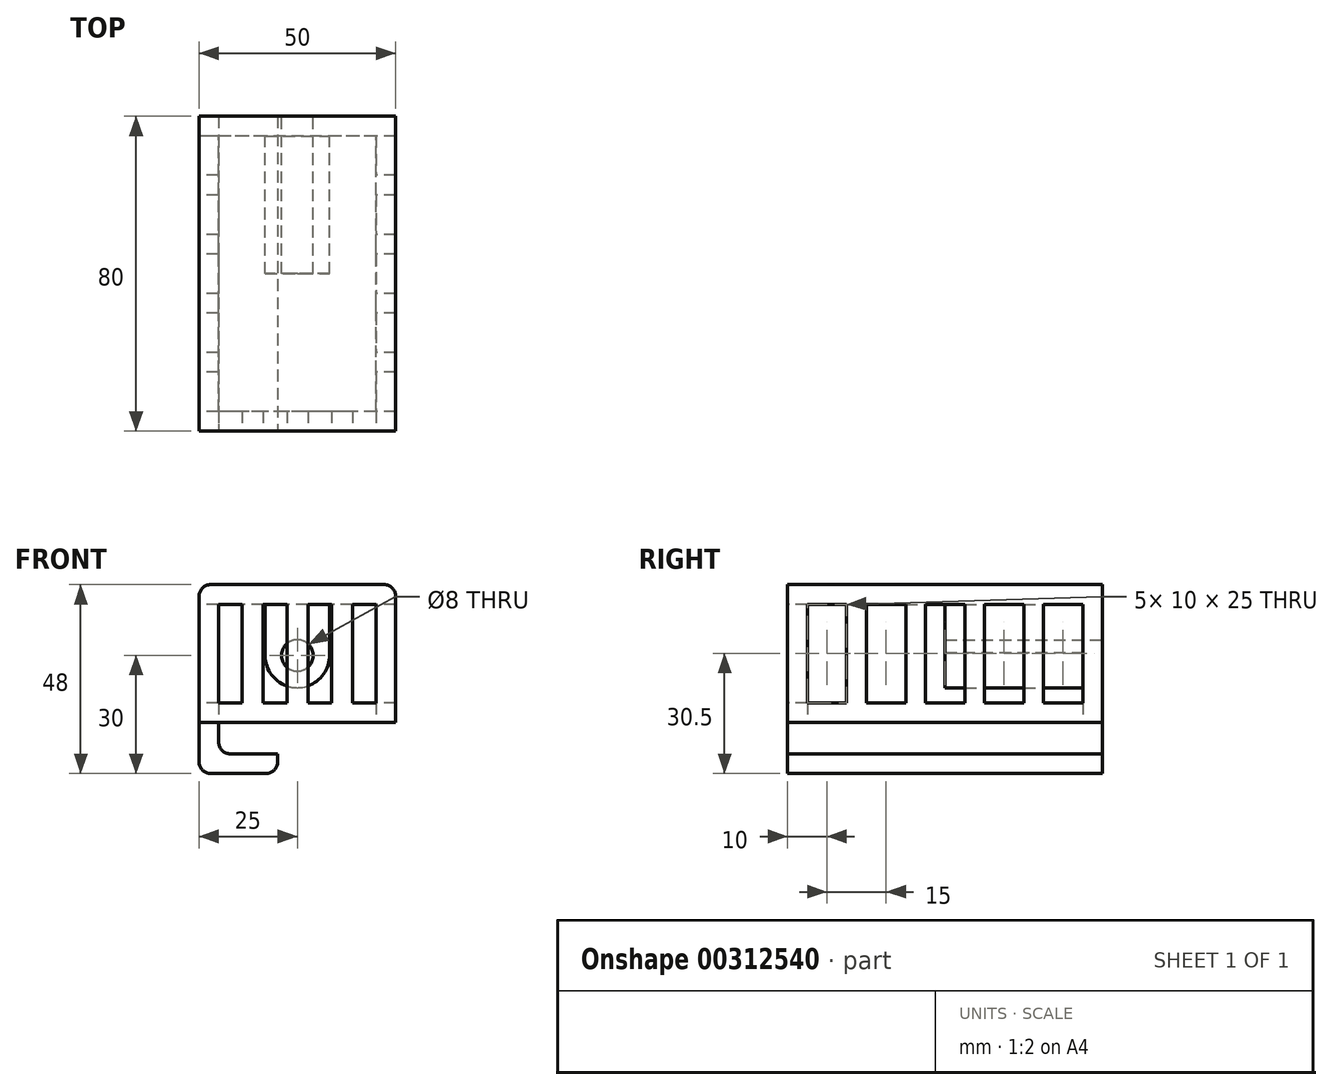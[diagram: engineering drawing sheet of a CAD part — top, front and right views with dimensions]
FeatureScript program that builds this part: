
annotation { "Feature Type Name" : "Feature", "Feature Type Description" : "" }
export const myFeature = defineFeature(function(context is Context, id is Id, definition is map)
    precondition{}
    {
        {
            var Q0;
            Q0=qCreatedBy(makeId("Top.planeOp"),FACE);
            var sketch = newSketch(context, id + "F0", { "sketchPlane" : qUnion([Q0])});
            skLineSegment(sketch, "E0.bottom", {"start": v(-50, 80) * mm, "end": v(0, 80) * mm});
            skLineSegment(sketch, "E0.top", {"start": v(-50, 0) * mm, "end": v(0, 0) * mm});
            skLineSegment(sketch, "E0.left", {"start": v(-50, 80) * mm, "end": v(-50, 0) * mm});
            skLineSegment(sketch, "E0.right", {"start": v(0, 80) * mm, "end": v(0, 0) * mm});
            skSolve(sketch);
        }
        {
            var Q0;
            Q0=qSketchRegion(id+"F0",true);
            extrude(context, id + "F1", {"entities" : qUnion([Q0]), "depth" : 35 * mm});
        }
        {
            var Q0;
            Q0=makeQuery(id+"F1.opExtrude","CAP_FACE",FACE,{"disambiguationData":[OSD([sQuery(id+"F0.wireOp",EDGE,"E0.bottom"),sQuery(id+"F0.wireOp",EDGE,"E0.top"),sQuery(id+"F0.wireOp",EDGE,"E0.left"),sQuery(id+"F0.wireOp",EDGE,"E0.right")])],"isStart":true});
            var sketch = newSketch(context, id + "F2", { "sketchPlane" : qUnion([Q0])});
            skLineSegment(sketch, "E1.bottom", {"start": v(-5, -5) * mm, "end": v(-45, -5) * mm});
            skLineSegment(sketch, "E1.top", {"start": v(-5, -75) * mm, "end": v(-45, -75) * mm});
            skLineSegment(sketch, "E1.left", {"start": v(-5, -5) * mm, "end": v(-5, -75) * mm});
            skLineSegment(sketch, "E1.right", {"start": v(-45, -5) * mm, "end": v(-45, -75) * mm});
            skSolve(sketch);
        }
        {
            var Q0;
            Q0=makeQuery(id+"F2.imprint","IMPRINT",FACE,{"disambiguationData":[TD([[makeQuery(id+"F2.imprint","IMPRINT",EDGE,{"derivedFrom":sQuery(id+"F2.wireOp",EDGE,"E1.bottom")}),1.0]])]});
            extrude(context, id + "F3", {"entities" : qUnion([Q0]), "operationType" : NewBodyOperationType.REMOVE, "oppositeDirection" : true, "depth" : 30 * mm});
        }
        {
            var Q0;
            Q0=makeQuery(id+"F1.opExtrude","SWEPT_FACE",FACE,{"disambiguationData":[OSD([sQuery(id+"F0.wireOp",EDGE,"E0.bottom")])]});
            var sketch = newSketch(context, id + "F4", { "sketchPlane" : qUnion([Q0])});
            skCircle(sketch, "E2", {"center": v(25, 17) * mm, "radius": 4 * mm});
            skSolve(sketch);
        }
        {
            var Q0;
            Q0=makeQuery(id+"F4.imprint","IMPRINT",FACE,{"disambiguationData":[TD([[makeQuery(id+"F4.imprint","IMPRINT",EDGE,{"derivedFrom":sQuery(id+"F4.wireOp",EDGE,"E2")}),1.0]])]});
            extrude(context, id + "F5", {"entities" : qUnion([Q0]), "operationType" : NewBodyOperationType.REMOVE, "endBound" : BoundingType.UP_TO_NEXT, "oppositeDirection" : true, "depth" : 25 * mm});
        }
        {
            var Q0;
            Q0=makeQuery(id+"F1.opExtrude","SWEPT_FACE",FACE,{"disambiguationData":[OSD([sQuery(id+"F0.wireOp",EDGE,"E0.left")])]});
            var sketch = newSketch(context, id + "F6", { "sketchPlane" : qUnion([Q0])});
            skLineSegment(sketch, "E3.bottom", {"start": v(-75, 30) * mm, "end": v(-65, 30) * mm});
            skLineSegment(sketch, "E3.top", {"start": v(-75, 5) * mm, "end": v(-65, 5) * mm});
            skLineSegment(sketch, "E3.left", {"start": v(-75, 30) * mm, "end": v(-75, 5) * mm});
            skLineSegment(sketch, "E3.right", {"start": v(-65, 30) * mm, "end": v(-65, 5) * mm});
            skLineSegment(sketch, "E4.1.0.0", {"start": v(-50, 30) * mm, "end": v(-50, 5) * mm});
            skLineSegment(sketch, "E4.1.0.1", {"start": v(-60, 30) * mm, "end": v(-50, 30) * mm});
            skLineSegment(sketch, "E4.1.0.2", {"start": v(-60, 30) * mm, "end": v(-60, 5) * mm});
            skLineSegment(sketch, "E4.1.0.3", {"start": v(-60, 5) * mm, "end": v(-50, 5) * mm});
            skLineSegment(sketch, "E4.2.0.0", {"start": v(-35, 30) * mm, "end": v(-35, 5) * mm});
            skLineSegment(sketch, "E4.2.0.1", {"start": v(-45, 30) * mm, "end": v(-35, 30) * mm});
            skLineSegment(sketch, "E4.2.0.2", {"start": v(-45, 30) * mm, "end": v(-45, 5) * mm});
            skLineSegment(sketch, "E4.2.0.3", {"start": v(-45, 5) * mm, "end": v(-35, 5) * mm});
            skLineSegment(sketch, "E4.3.0.0", {"start": v(-20, 30) * mm, "end": v(-20, 5) * mm});
            skLineSegment(sketch, "E4.3.0.1", {"start": v(-30, 30) * mm, "end": v(-20, 30) * mm});
            skLineSegment(sketch, "E4.3.0.2", {"start": v(-30, 30) * mm, "end": v(-30, 5) * mm});
            skLineSegment(sketch, "E4.3.0.3", {"start": v(-30, 5) * mm, "end": v(-20, 5) * mm});
            skLineSegment(sketch, "E4.4.0.0", {"start": v(-5, 30) * mm, "end": v(-5, 5) * mm});
            skLineSegment(sketch, "E4.4.0.1", {"start": v(-15, 30) * mm, "end": v(-5, 30) * mm});
            skLineSegment(sketch, "E4.4.0.2", {"start": v(-15, 30) * mm, "end": v(-15, 5) * mm});
            skLineSegment(sketch, "E4.4.0.3", {"start": v(-15, 5) * mm, "end": v(-5, 5) * mm});
            skLineSegment(sketch, "E4.direction1", {"start": v(-65, 5) * mm, "end": v(-50, 5) * mm, "construction": true});
            skSolve(sketch);
        }
        {
            var Q0;
            Q0=qSketchRegion(id+"F6",true);
            extrude(context, id + "F7", {"entities" : qUnion([Q0]), "operationType" : NewBodyOperationType.REMOVE, "endBound" : BoundingType.THROUGH_ALL, "oppositeDirection" : true, "depth" : 25 * mm});
        }
        {
            var Q0;
            Q0=makeQuery(id+"F1.opExtrude","SWEPT_FACE",FACE,{"disambiguationData":[OSD([sQuery(id+"F0.wireOp",EDGE,"E0.top")])]});
            var sketch = newSketch(context, id + "F8", { "sketchPlane" : qUnion([Q0])});
            skLineSegment(sketch, "E5.bottom", {"start": v(-45, 30) * mm, "end": v(-39, 30) * mm});
            skLineSegment(sketch, "E5.top", {"start": v(-45, 5) * mm, "end": v(-39, 5) * mm});
            skLineSegment(sketch, "E5.left", {"start": v(-45, 30) * mm, "end": v(-45, 5) * mm});
            skLineSegment(sketch, "E5.right", {"start": v(-39, 30) * mm, "end": v(-39, 5) * mm});
            skLineSegment(sketch, "E6.1.0.0", {"start": v(-33.67, 30) * mm, "end": v(-27.67, 30) * mm});
            skLineSegment(sketch, "E6.1.0.1", {"start": v(-27.67, 30) * mm, "end": v(-27.67, 5) * mm});
            skLineSegment(sketch, "E6.1.0.2", {"start": v(-33.67, 30) * mm, "end": v(-33.67, 5) * mm});
            skLineSegment(sketch, "E6.1.0.3", {"start": v(-33.67, 5) * mm, "end": v(-27.67, 5) * mm});
            skLineSegment(sketch, "E6.2.0.0", {"start": v(-22.33, 30) * mm, "end": v(-16.33, 30) * mm});
            skLineSegment(sketch, "E6.2.0.1", {"start": v(-16.33, 30) * mm, "end": v(-16.33, 5) * mm});
            skLineSegment(sketch, "E6.2.0.2", {"start": v(-22.33, 30) * mm, "end": v(-22.33, 5) * mm});
            skLineSegment(sketch, "E6.2.0.3", {"start": v(-22.33, 5) * mm, "end": v(-16.33, 5) * mm});
            skLineSegment(sketch, "E6.3.0.0", {"start": v(-11, 30) * mm, "end": v(-5, 30) * mm});
            skLineSegment(sketch, "E6.3.0.1", {"start": v(-5, 30) * mm, "end": v(-5, 5) * mm});
            skLineSegment(sketch, "E6.3.0.2", {"start": v(-11, 30) * mm, "end": v(-11, 5) * mm});
            skLineSegment(sketch, "E6.3.0.3", {"start": v(-11, 5) * mm, "end": v(-5, 5) * mm});
            skLineSegment(sketch, "E6.direction1", {"start": v(-45, 5) * mm, "end": v(-33.67, 5) * mm, "construction": true});
            skSolve(sketch);
        }
        {
            var Q0;
            Q0=qSketchRegion(id+"F8",true);
            extrude(context, id + "F9", {"entities" : qUnion([Q0]), "operationType" : NewBodyOperationType.REMOVE, "endBound" : BoundingType.UP_TO_NEXT, "oppositeDirection" : true, "depth" : 25 * mm});
        }
        {
            var Q0;
            Q0=qCreatedBy(makeId("Front.planeOp"),FACE);
            cPlane(context, id + "F10", {"entities" : qUnion([Q0]), "cplaneType" : CPlaneType.OFFSET, "offset" : 50 * mm, "oppositeDirection" : true, "width" : 150 * mm, "height" : 150 * mm});
        }
        {
            var Q0;
            Q0=qCreatedBy(id+"F10.planeOp",FACE);
            var sketch = newSketch(context, id + "F11", { "sketchPlane" : qUnion([Q0])});
            skCircle(sketch, "E7", {"center": v(-25, 17) * mm, "radius": 4 * mm});
            skArc(sketch, "E8", {"start": v(-33.16, 17.71) * mm, "mid": v(-25.36, 8.82) * mm, "end": v(-16.81, 17) * mm});
            skLineSegment(sketch, "E9", {"start": v(-16.81, 17) * mm, "end": v(-16.81, 35) * mm});
            skLineSegment(sketch, "E10", {"start": v(-33.16, 17.71) * mm, "end": v(-33.16, 35) * mm});
            skLineSegment(sketch, "E11", {"start": v(-33.16, 35) * mm, "end": v(-16.81, 35) * mm});
            skSolve(sketch);
        }
        {
            var Q0;
            Q0=makeQuery(id+"F11.imprint","IMPRINT",FACE,{"disambiguationData":[TD([[makeQuery(id+"F11.imprint","IMPRINT",EDGE,{"derivedFrom":sQuery(id+"F11.wireOp",EDGE,"E7")}),-1.0]])]});
            extrude(context, id + "F12", {"entities" : qUnion([Q0]), "operationType" : NewBodyOperationType.ADD, "depth" : 10 * mm});
        }
        {
            var Q0;
            Q0=qCreatedBy(makeId("Front.planeOp"),FACE);
            var sketch = newSketch(context, id + "F13", { "sketchPlane" : qUnion([Q0])});
            skLineSegment(sketch, "E12.bottom", {"start": v(-45, 0) * mm, "end": v(-50, 0) * mm});
            skLineSegment(sketch, "E12.top", {"start": v(-45, -13) * mm, "end": v(-50, -13) * mm});
            skLineSegment(sketch, "E12.left", {"start": v(-45, 0) * mm, "end": v(-45, -13) * mm});
            skLineSegment(sketch, "E12.right", {"start": v(-50, 0) * mm, "end": v(-50, -13) * mm});
            skLineSegment(sketch, "E13.bottom", {"start": v(-45, -13) * mm, "end": v(-30, -13) * mm});
            skLineSegment(sketch, "E13.top", {"start": v(-45, -8) * mm, "end": v(-30, -8) * mm});
            skLineSegment(sketch, "E13.left", {"start": v(-45, -13) * mm, "end": v(-45, -8) * mm});
            skLineSegment(sketch, "E13.right", {"start": v(-30, -13) * mm, "end": v(-30, -8) * mm});
            skSolve(sketch);
        }
        {
            var Q0;
            Q0=qSketchRegion(id+"F13",true);
            extrude(context, id + "F14", {"entities" : qUnion([Q0]), "oppositeDirection" : true, "depth" : 80 * mm});
        }
        {
            var Q0;
            Q0=makeQuery(id+"F14.opExtrude","SWEPT_EDGE",EDGE,{"disambiguationData":[OSD([sQuery(id+"F13.wireOp",EDGE,"E12.left"),sQuery(id+"F13.wireOp",EDGE,"E13.top"),sQuery(id+"F13.wireOp",EDGE,"E13.left")])]});
            var Q1;
            Q1=makeQuery(id+"F14.opExtrude","SWEPT_EDGE",EDGE,{"disambiguationData":[OSD([sQuery(id+"F13.wireOp",EDGE,"E12.top"),sQuery(id+"F13.wireOp",EDGE,"E12.right")])]});
            var Q2;
            Q2=makeQuery(id+"F14.opExtrude","SWEPT_EDGE",EDGE,{"disambiguationData":[OSD([sQuery(id+"F13.wireOp",EDGE,"E13.bottom"),sQuery(id+"F13.wireOp",EDGE,"E13.right")])]});
            var Q3;
            Q3=makeQuery(id+"F1.opExtrude","CAP_EDGE",EDGE,{"disambiguationData":[OSD([sQuery(id+"F0.wireOp",EDGE,"E0.left")])],"isStart":false});
            var Q4;
            Q4=makeQuery(id+"F1.opExtrude","CAP_EDGE",EDGE,{"disambiguationData":[OSD([sQuery(id+"F0.wireOp",EDGE,"E0.right")])],"isStart":false});
            fillet(context, id + "F15", {"entities" : qUnion([Q0, Q1, Q2, Q3, Q4]), "radius" : 3 * mm, "tangentPropagation" : true, "allowEdgeOverflow" : false});
        }
        {
            var Q0;
            Q0 = qSketchRegion(id + "F11", true);
            extrude(context, id + "F16", {"entities" : qUnion([Q0]), "operationType" : NewBodyOperationType.ADD, "oppositeDirection" : true, "depth" : 25 * mm});
        }
    });
